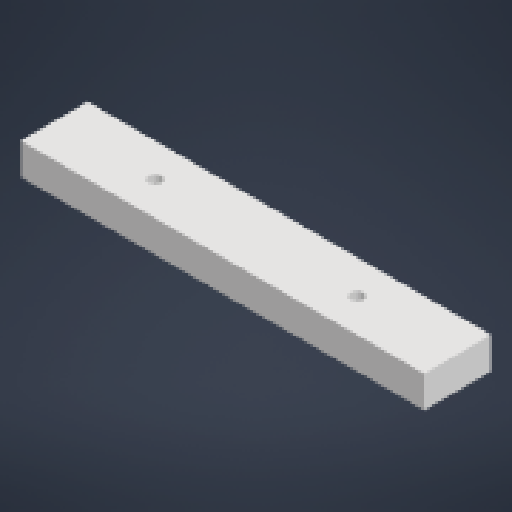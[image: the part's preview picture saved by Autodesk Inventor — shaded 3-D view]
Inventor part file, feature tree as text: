
AUTODESK INVENTOR PART (.ipt)
format: ipt  version: 2023 (Build 270158000, 158)  size: 119,296 bytes
history: native  units: in
note: dims shown in document units (in); Inventor stores cm internally (conversion verified against a paired STEP export)
features: extrude x1, sketch x1
ambient origin geometry x8: Origin, YZ Plane, XZ Plane, XY Plane, X Axis, Y Axis, Z Axis, Center Point
bodies: Solid1 (feature_tree)
feature tree (2):
  extrude  "Extrusion1"  Depth=1.0in
  sketch  "Sketch1"  dims[d0=6.0in d1=1.0in d10=1.5in d11=0.1875in d12=0.47in d13=0.0in]
